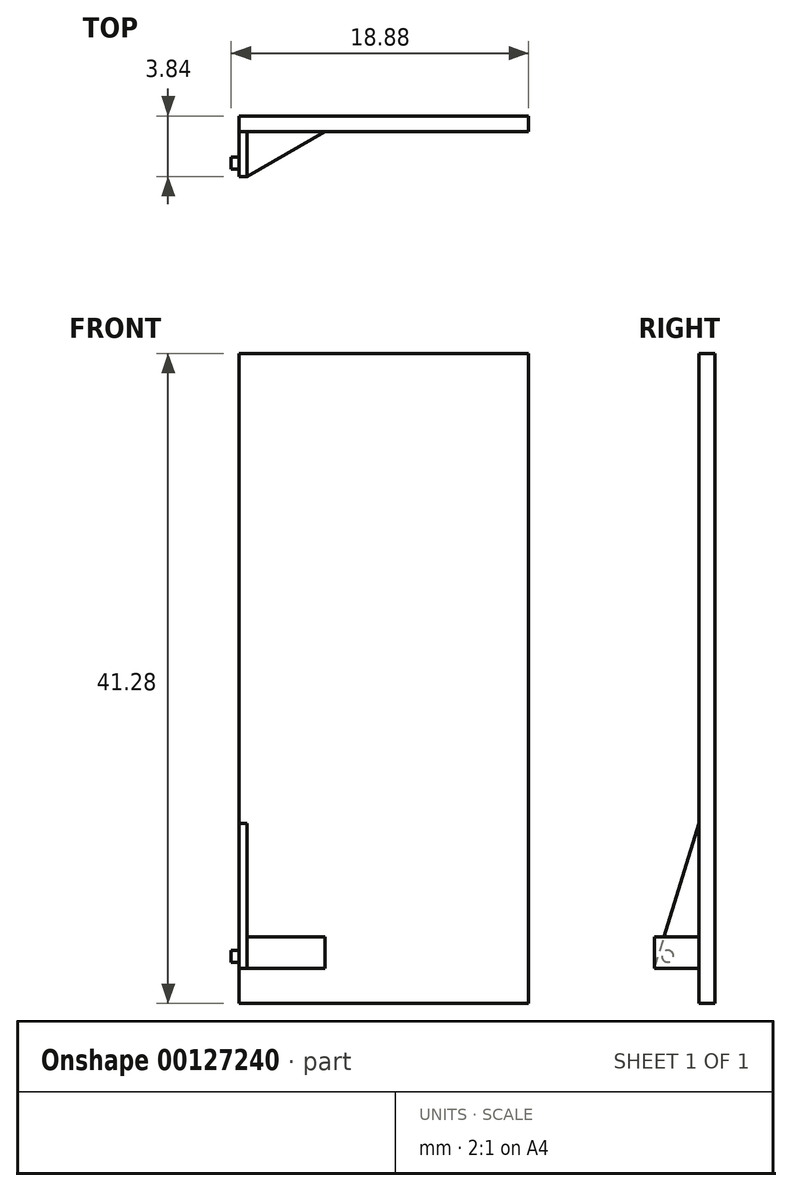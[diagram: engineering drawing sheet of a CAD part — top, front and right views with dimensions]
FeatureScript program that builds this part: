
annotation { "Feature Type Name" : "Feature", "Feature Type Description" : "" }
export const myFeature = defineFeature(function(context is Context, id is Id, definition is map)
    precondition{}
    {
        {
            var Q0;
            Q0=qCreatedBy(makeId("Front.planeOp"),FACE);
            var sketch = newSketch(context, id + "F0", { "sketchPlane" : qUnion([Q0])});
            skLineSegment(sketch, "E0.bottom", {"start": v(0, 0) * mm, "end": v(-18.38, 0) * mm});
            skLineSegment(sketch, "E0.top", {"start": v(0, 41.28) * mm, "end": v(-18.38, 41.28) * mm});
            skLineSegment(sketch, "E0.left", {"start": v(0, 0) * mm, "end": v(0, 41.28) * mm});
            skLineSegment(sketch, "E0.right", {"start": v(-18.38, 0) * mm, "end": v(-18.38, 41.28) * mm});
            skSolve(sketch);
        }
        {
            var Q0;
            Q0=makeQuery(id+"F0.imprint","IMPRINT",FACE,{"disambiguationData":[TD([[makeQuery(id+"F0.imprint","IMPRINT",EDGE,{"derivedFrom":sQuery(id+"F0.wireOp",EDGE,"E0.bottom")}),-1.0]])]});
            extrude(context, id + "F1", {"entities" : qUnion([Q0]), "depth" : 1 * mm});
        }
        {
            var Q0;
            Q0=makeQuery(id+"F1.opExtrude","SWEPT_FACE",FACE,{"disambiguationData":[OSD([sQuery(id+"F0.wireOp",EDGE,"E0.right")])]});
            var sketch = newSketch(context, id + "F2", { "sketchPlane" : qUnion([Q0])});
            skLineSegment(sketch, "E1", {"start": v(0, 2.23) * mm, "end": v(3.84, 2.23) * mm});
            skLineSegment(sketch, "E2", {"start": v(3.84, 2.23) * mm, "end": v(1, 11.45) * mm});
            skLineSegment(sketch, "E3", {"start": v(1, 11.45) * mm, "end": v(0, 11.45) * mm});
            skLineSegment(sketch, "E4", {"start": v(0, 11.45) * mm, "end": v(0, 2.23) * mm});
            skSolve(sketch);
        }
        {
            var Q0;
            {var subQ0=sQuery(id+"F2.wireOp",EDGE,"E2");Q0=makeQuery(id+"F2.imprint","IMPRINT",FACE,{"disambiguationData":[TD([[makeQuery(id+"F2.imprint","IMPRINT",EDGE,{"derivedFrom":subQ0}),1.0]])]});}
            extrude(context, id + "F3", {"entities" : qUnion([Q0]), "operationType" : NewBodyOperationType.ADD, "oppositeDirection" : true, "depth" : 0.5 * mm});
        }
        {
            var Q0;
            {var subQ0=sQuery(id+"F0.wireOp",EDGE,"E0.right");Q0=makeQuery(id+"F3.boolean.opBoolean","MERGE",FACE,{"derivedFrom":[makeQuery(id+"F1.opExtrude","SWEPT_FACE",FACE,{"disambiguationData":[OSD([subQ0])]}),makeQuery(id+"F3.opExtrude","CAP_FACE",FACE,{"disambiguationData":[OSD([subQ0,sQuery(id+"F2.wireOp",EDGE,"E1"),sQuery(id+"F2.wireOp",EDGE,"E2")])],"isStart":true})]});}
            var sketch = newSketch(context, id + "F4", { "sketchPlane" : qUnion([Q0])});
            skCircle(sketch, "E5", {"center": v(3, 3) * mm, "radius": 0.38 * mm});
            skSolve(sketch);
        }
        {
            var Q0;
            Q0 = qSketchRegion(id + "F4", true);
            extrude(context, id + "F5", {"entities" : qUnion([Q0]), "operationType" : NewBodyOperationType.ADD, "depth" : .5 * mm});
        }
        {
            var Q0;
            Q0=makeQuery(id+"F3.opExtrude","SWEPT_FACE",FACE,{"disambiguationData":[OSD([sQuery(id+"F2.wireOp",EDGE,"E1")])]});
            var sketch = newSketch(context, id + "F6", { "sketchPlane" : qUnion([Q0])});
            skLineSegment(sketch, "E6", {"start": v(-17.88, 3.84) * mm, "end": v(-12.8, 0.92) * mm});
            skLineSegment(sketch, "E7", {"start": v(-12.8, 0.92) * mm, "end": v(-17.88, 0.46) * mm});
            skLineSegment(sketch, "E8", {"start": v(-17.88, 0.46) * mm, "end": v(-17.88, 3.84) * mm});
            skSolve(sketch);
        }
        {
            var Q0;
            {var subQ0=sQuery(id+"F6.wireOp",EDGE,"E6");Q0=makeQuery(id+"F6.imprint","IMPRINT",FACE,{"disambiguationData":[TD([[makeQuery(id+"F6.imprint","IMPRINT",EDGE,{"derivedFrom":subQ0}),-1.0]])]});}
            extrude(context, id + "F7", {"entities" : qUnion([Q0]), "operationType" : NewBodyOperationType.ADD, "oppositeDirection" : true, "depth" : 2 * mm});
        }
    });
